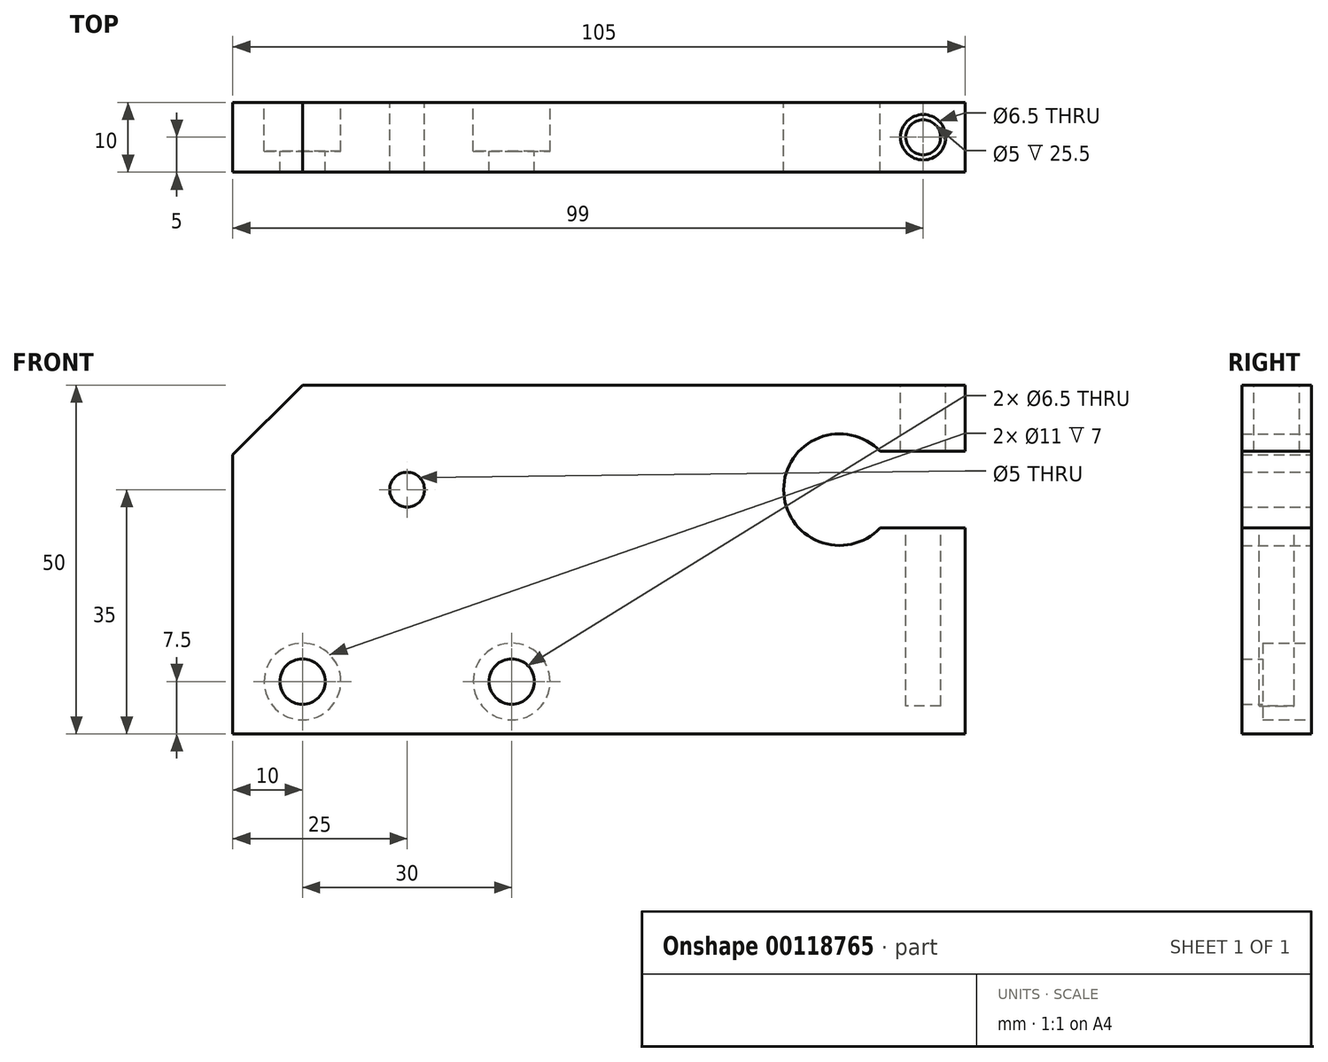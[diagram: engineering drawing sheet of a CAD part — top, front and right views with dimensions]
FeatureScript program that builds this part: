
annotation { "Feature Type Name" : "Feature", "Feature Type Description" : "" }
export const myFeature = defineFeature(function(context is Context, id is Id, definition is map)
    precondition{}
    {
        {
            var Q0;
            Q0=qCreatedBy(makeId("Front.planeOp"),FACE);
            var sketch = newSketch(context, id + "F0", { "sketchPlane" : qUnion([Q0])});
            skLineSegment(sketch, "E0.bottom", {"start": v(-52.5, -25) * mm, "end": v(52.5, -25) * mm});
            skLineSegment(sketch, "E0.top", {"start": v(-52.5, 25) * mm, "end": v(52.5, 25) * mm});
            skLineSegment(sketch, "E0.left", {"start": v(-52.5, -25) * mm, "end": v(-52.5, 25) * mm});
            skLineSegment(sketch, "E0.right", {"start": v(52.5, -25) * mm, "end": v(52.5, 25) * mm});
            skPoint(sketch, "E0.middle", {"position": v(0, 0) * mm});
            skLineSegment(sketch, "E1", {"start": v(-42.5, -25) * mm, "end": v(-42.5, -17.5) * mm});
            skLineSegment(sketch, "E2", {"start": v(-42.5, -17.5) * mm, "end": v(-12.5, -17.5) * mm});
            skCircle(sketch, "E3", {"center": v(-42.5, -17.5) * mm, "radius": 3.25 * mm});
            skCircle(sketch, "E4", {"center": v(-12.5, -17.5) * mm, "radius": 3.25 * mm});
            skLineSegment(sketch, "E5", {"start": v(-27.5, 25) * mm, "end": v(-27.5, 10) * mm});
            skCircle(sketch, "E6", {"center": v(-27.5, 10) * mm, "radius": 2.5 * mm});
            skCircle(sketch, "E7", {"center": v(34.5, 10) * mm, "radius": 8 * mm});
            skLineSegment(sketch, "E8", {"start": v(47.24, 4.5) * mm, "end": v(40.3, 4.5) * mm});
            skLineSegment(sketch, "E9", {"start": v(47.24, 15.5) * mm, "end": v(40.3, 15.5) * mm});
            skLineSegment(sketch, "E10", {"start": v(47.24, 15.5) * mm, "end": v(52.5, 15.5) * mm});
            skLineSegment(sketch, "E11", {"start": v(52.5, 4.5) * mm, "end": v(47.24, 4.5) * mm});
            skSolve(sketch);
        }
        {
            var Q0;
            {var subQ7=sQuery(id+"F0.wireOp",EDGE,"E0.left");Q0=makeQuery(id+"F0.imprint","IMPRINT",FACE,{"disambiguationData":[TD([[makeQuery(id+"F0.imprint","IMPRINT",EDGE,{"derivedFrom":subQ7}),-1.0]])]});}
            extrude(context, id + "F1", {"entities" : qUnion([Q0]), "depth" : 10 * mm});
        }
        {
            var Q0;
            Q0=makeQuery(id+"F1.opExtrude","SWEPT_EDGE",EDGE,{"disambiguationData":[OSD([sQuery(id+"F0.wireOp",EDGE,"E0.top"),sQuery(id+"F0.wireOp",EDGE,"E0.left")])]});
            chamfer(context, id + "F2", {"entities" : qUnion([Q0]), "width" : 10 * mm, "tangentPropagation" : true});
        }
        {
            var Q0;
            Q0=makeQuery(id+"F1.opExtrude","CAP_FACE",FACE,{"disambiguationData":[OSD([sQuery(id+"F0.wireOp",EDGE,"E0.bottom"),sQuery(id+"F0.wireOp",EDGE,"E0.top"),sQuery(id+"F0.wireOp",EDGE,"E0.left"),sQuery(id+"F0.wireOp",EDGE,"E0.right"),sQuery(id+"F0.wireOp",EDGE,"E3"),sQuery(id+"F0.wireOp",EDGE,"E4"),sQuery(id+"F0.wireOp",EDGE,"E6"),sQuery(id+"F0.wireOp",EDGE,"E7"),sQuery(id+"F0.wireOp",EDGE,"E8"),sQuery(id+"F0.wireOp",EDGE,"E9"),sQuery(id+"F0.wireOp",EDGE,"E10"),sQuery(id+"F0.wireOp",EDGE,"E11")])],"isStart":true});
            var sketch = newSketch(context, id + "F3", { "sketchPlane" : qUnion([Q0])});
            skCircle(sketch, "E12", {"center": v(12.5, -17.5) * mm, "radius": 5.5 * mm});
            skCircle(sketch, "E13", {"center": v(42.5, -17.5) * mm, "radius": 5.5 * mm});
            skSolve(sketch);
        }
        {
            var Q0;
            Q0 = qSketchRegion(id + "F3", true);
            extrude(context, id + "F4", {"entities" : qUnion([Q0]), "operationType" : NewBodyOperationType.REMOVE, "oppositeDirection" : true, "depth" : 7 * mm});
        }
        {
            var Q0;
            Q0=makeQuery(id+"F1.opExtrude","SWEPT_FACE",FACE,{"disambiguationData":[OSD([sQuery(id+"F0.wireOp",EDGE,"E0.top")])]});
            var sketch = newSketch(context, id + "F5", { "sketchPlane" : qUnion([Q0])});
            skLineSegment(sketch, "E14", {"start": v(52.5, -5) * mm, "end": v(46.5, -5) * mm});
            skCircle(sketch, "E15", {"center": v(46.5, -5) * mm, "radius": 3.25 * mm});
            skSolve(sketch);
        }
        {
            var Q0;
            Q0 = qSketchRegion(id + "F5", true);
            extrude(context, id + "F6", {"entities" : qUnion([Q0]), "operationType" : NewBodyOperationType.REMOVE, "oppositeDirection" : true, "depth" : 15 * mm});
        }
        {
            var Q0;
            Q0=makeQuery(id+"F1.opExtrude","SWEPT_FACE",FACE,{"disambiguationData":[OSD([sQuery(id+"F0.wireOp",EDGE,"E0.top")])]});
            var sketch = newSketch(context, id + "F7", { "sketchPlane" : qUnion([Q0])});
            skCircle(sketch, "E16", {"center": v(46.5, -5) * mm, "radius": 2.5 * mm});
            skSolve(sketch);
        }
        {
            var Q0;
            Q0=makeQuery(id+"F7.imprint","IMPRINT",FACE,{"disambiguationData":[TD([[makeQuery(id+"F7.imprint","IMPRINT",EDGE,{"derivedFrom":sQuery(id+"F7.wireOp",EDGE,"E16")}),1.0]])]});
            extrude(context, id + "F8", {"entities" : qUnion([Q0]), "operationType" : NewBodyOperationType.REMOVE, "oppositeDirection" : true, "depth" : 46 * mm});
        }
    });
